# Revit family: LQ4020001_Teleducha Liquid
name_source: partatom
category: Plumbing Fixtures
units: mm (PartAtom-declared; Revit-internal decimal feet)

## family parameters
Always vertical = Yes
Cut with Voids When Loaded = No
OmniClass Number = 23.31.11.00
OmniClass Title = Faucets
Part Type = Normal
Room Calculation Point = No
Round Connector Dimension = Use Diameter
Shared = No
Work Plane-Based = No

## types (1)
- Teleducha Liquid
    Alto = 242 mm
    Ancho = 110 mm  [stored 0.360892 ft]
    Capacidad de flujo = A 80 psi: 9.3 L/min.
    Creado por = BIMB0AU
    Default Elevation = 0 mm  [stored 0 ft]
    Description = La teleducha liquid con diámetro medio ofrece cobertura total gracias a sus múltiples chorros para una relajación completa, con botón selector de funciones ue hace más fácil operar el camnio entre los chorros ofreciendo mauor confort en la ducha.
    Dimensiones generales del producto = 65 x 165 x 260 mm.
    Diámetro = 13 mm
    Fecha de creación = 02/07/2021
    Garantía = 30 años - 2 años Acabados.
    Manufacturer = Corona.
    Material = Corona_Cromado
    Material 2 = Corona_Plastico_Gris
    Model = LQ4020001_Teleducha Liquid.
    Peso neto = 470 gr. / 1.03 lb.
    Presión máxima recomendada = 125 psi (860 kPa).
    Presión mínima recomendada = 20 psi (140 kPa).
    Profundidad = 55 mm  [stored 0.180446 ft]
    Recubrimientos = Resistente a la corrosión, pelado y decoloración por agua. Recubrimientos no tóxicos. Producto para uso doméstico.
    Temperatura de uso = 5° C a 71° C.

note: [stored X ft] marks values corroborated as IEEE doubles in the binary element streams (Revit-internal decimal feet)

## geometry (parser evidence)
native form markers: Sweep x2
no freeform markers — native parametric forms only
